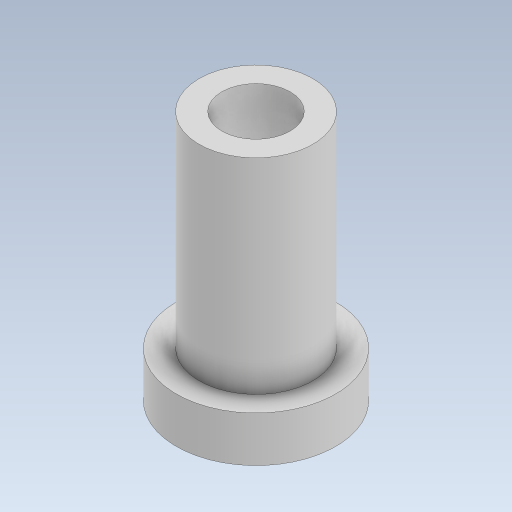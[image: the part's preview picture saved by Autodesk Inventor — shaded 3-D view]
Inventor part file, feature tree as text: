
AUTODESK INVENTOR PART (.ipt)
format: ipt  version: 2023.5 (Build 275446000, 446)  size: 276,992 bytes
history: native  units: mm
features: extrude x3, sketch x2
ambient origin geometry x8: Origin, YZ Plane, XZ Plane, XY Plane, X Axis, Y Axis, Z Axis, Center Point
bodies: Solid1 (feature_tree)
feature tree (5):
  sketch  "Sketch1"  dims[d0=7.0mm d1=5.0mm]
  extrude  "Extrusion1"  Depth=7.0mm
  extrude  "Extrusion2"  Depth=2.0mm TaperAngle=0.0deg
  extrude  "Extrusion3"  Depth=7.0mm
  sketch  "Sketch2"  dims[d2=11.0mm d3=0.0mm d4=2.0mm d5=0.0mm d6=3.0mm d7=7.0mm d8=0.0mm]
